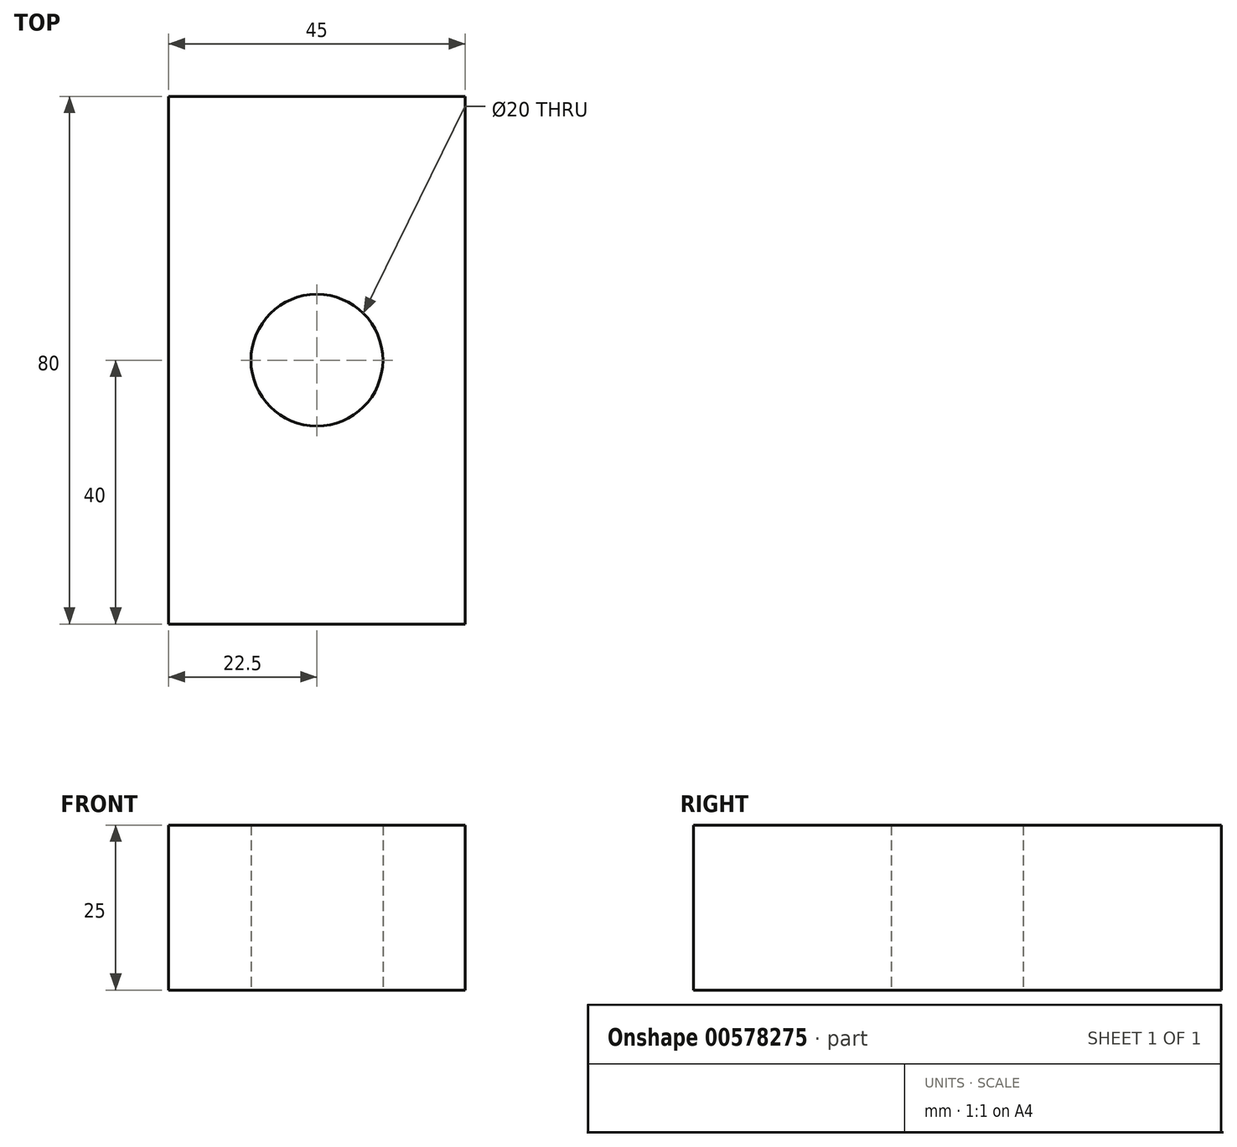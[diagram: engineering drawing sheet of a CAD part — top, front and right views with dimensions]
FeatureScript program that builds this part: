
annotation { "Feature Type Name" : "Feature", "Feature Type Description" : "" }
export const myFeature = defineFeature(function(context is Context, id is Id, definition is map)
    precondition{}
    {
        {
            var Q0;
            Q0=qCreatedBy(makeId("Top.planeOp"),FACE);
            var sketch = newSketch(context, id + "F0", { "sketchPlane" : qUnion([Q0])});
            skLineSegment(sketch, "E0.bottom", {"start": v(-22.5, 40) * mm, "end": v(22.5, 40) * mm});
            skLineSegment(sketch, "E0.top", {"start": v(-22.5, -40) * mm, "end": v(22.5, -40) * mm});
            skLineSegment(sketch, "E0.left", {"start": v(-22.5, 40) * mm, "end": v(-22.5, -40) * mm});
            skLineSegment(sketch, "E0.right", {"start": v(22.5, 40) * mm, "end": v(22.5, -40) * mm});
            skPoint(sketch, "E0.middle", {"position": v(0, 0) * mm});
            skCircle(sketch, "E1", {"center": v(0, 0) * mm, "radius": 10 * mm});
            skSolve(sketch);
        }
        {
            var Q0;
            Q0 = qSketchRegion(id + "F0", true);
            extrude(context, id + "F1", {"entities" : qUnion([Q0]), "depth" : 25 * mm, "offsetDistance" : 25 * mm});
        }
    });
